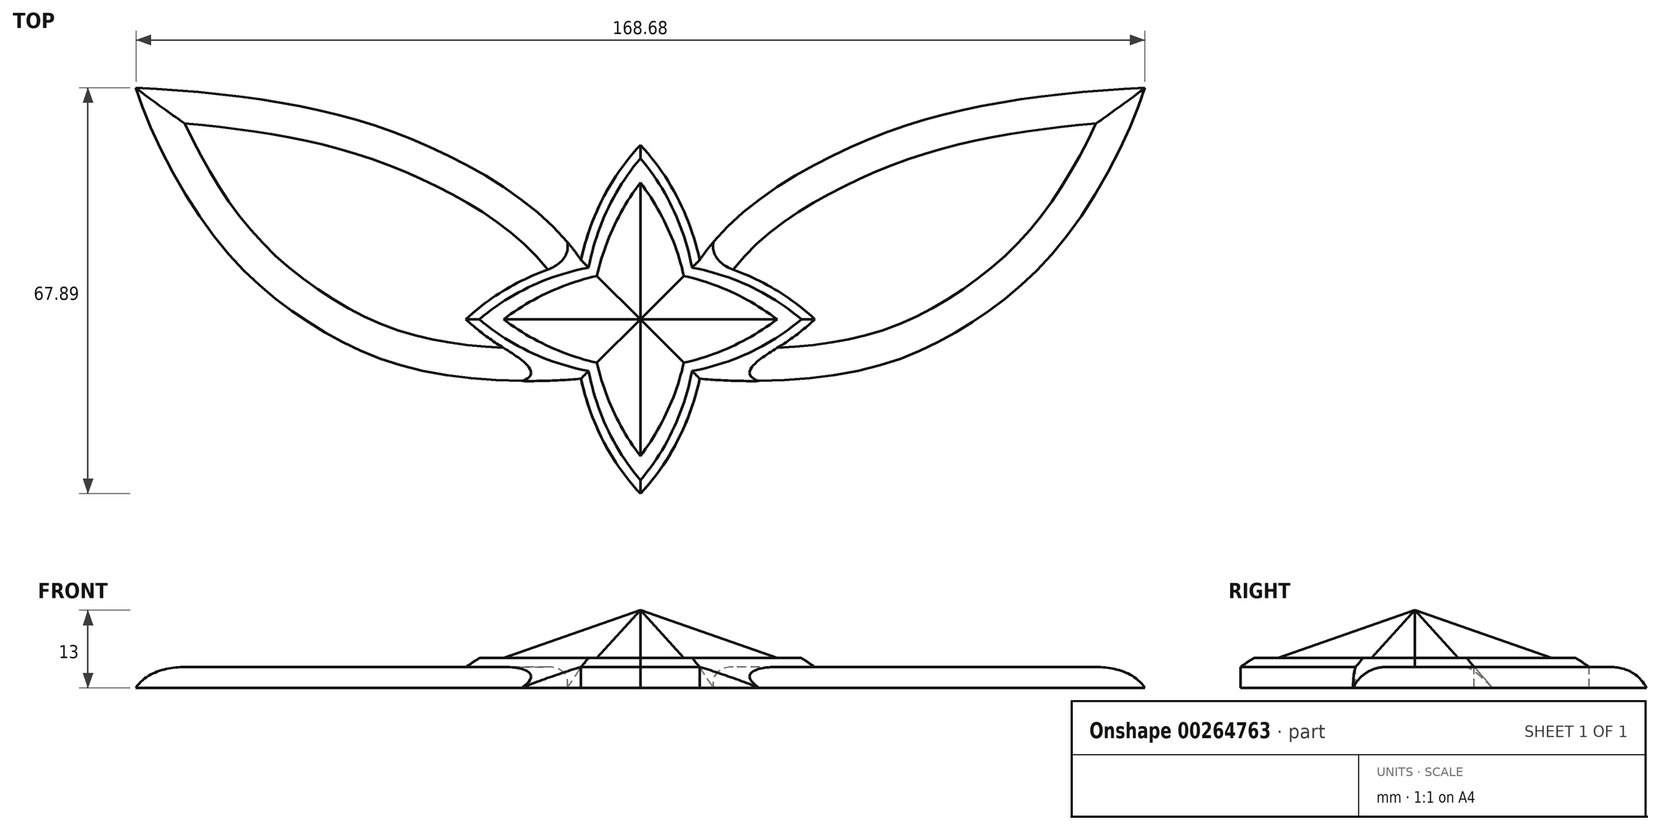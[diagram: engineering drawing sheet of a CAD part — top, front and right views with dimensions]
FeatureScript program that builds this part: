
annotation { "Feature Type Name" : "Feature", "Feature Type Description" : "" }
export const myFeature = defineFeature(function(context is Context, id is Id, definition is map)
    precondition{}
    {
        {
            var Q0;
            Q0=qCreatedBy(makeId("Top.planeOp"),FACE);
            var sketch = newSketch(context, id + "F0", { "sketchPlane" : qUnion([Q0])});
            skLineSegment(sketch, "E0", {"start": v(0, 27.96) * mm, "end": v(0, -27.04) * mm, "construction": true});
            skSolve(sketch);
        }
        {
            var Q0;
            Q0=qCreatedBy(makeId("Top.planeOp"),FACE);
            var sketch = newSketch(context, id + "F1", { "sketchPlane" : qUnion([Q0])});
            skFitSpline(sketch, "E1", {"points": [v(0, 22.87) * mm, v(-7.26, 7.26) * mm], "startDerivative": vector(-10.3, -13.5) * mm, "endDerivative": vector(-3.62, -16.65) * mm});
            skLineSegment(sketch, "E2", {"start": v(-7.26, 7.26) * mm, "end": v(0, 0) * mm, "construction": true});
            skFitSpline(sketch, "E3.MirrorCS", {"points": [v(0, 22.87) * mm, v(7.26, 7.26) * mm], "startDerivative": vector(10.3, -13.5) * mm, "endDerivative": vector(3.62, -16.65) * mm});
            skLineSegment(sketch, "E4.MirrorCS", {"start": v(7.26, 7.26) * mm, "end": v(0, 0) * mm, "construction": true});
            skFitSpline(sketch, "E5.MirrorCS", {"points": [v(-22.87, 0) * mm, v(-7.26, 7.26) * mm], "startDerivative": vector(13.5, 10.3) * mm, "endDerivative": vector(16.65, 3.62) * mm});
            skFitSpline(sketch, "E6.MirrorCS", {"points": [v(-22.87, 0) * mm, v(-7.26, -7.26) * mm], "startDerivative": vector(13.5, -10.3) * mm, "endDerivative": vector(16.65, -3.62) * mm});
            skFitSpline(sketch, "E7.MirrorCS", {"points": [v(22.87, 0) * mm, v(7.26, 7.26) * mm], "startDerivative": vector(-13.5, 10.3) * mm, "endDerivative": vector(-16.65, 3.62) * mm});
            skFitSpline(sketch, "E8.MirrorCS", {"points": [v(22.87, 0) * mm, v(7.26, -7.26) * mm], "startDerivative": vector(-13.5, -10.3) * mm, "endDerivative": vector(-16.65, -3.62) * mm});
            skFitSpline(sketch, "E9.MirrorCS", {"points": [v(0, -22.87) * mm, v(7.26, -7.26) * mm], "startDerivative": vector(10.3, 13.5) * mm, "endDerivative": vector(3.62, 16.65) * mm});
            skFitSpline(sketch, "E10.MirrorCS", {"points": [v(0, -22.87) * mm, v(-7.26, -7.26) * mm], "startDerivative": vector(-10.3, 13.5) * mm, "endDerivative": vector(-3.62, 16.65) * mm});
            skSolve(sketch);
        }
        {
            var Q0;
            Q0=qCreatedBy(makeId("Top.planeOp"),FACE);
            cPlane(context, id + "F2", {"entities" : qUnion([Q0]), "cplaneType" : CPlaneType.OFFSET, "offset" : 8 * mm, "width" : 150 * mm, "height" : 150 * mm});
        }
        {
            var Q0;
            Q0=qCreatedBy(id+"F2.planeOp",FACE);
            var sketch = newSketch(context, id + "F3", { "sketchPlane" : qUnion([Q0])});
            skPoint(sketch, "E11", {"position": v(0, 0) * mm});
            skSolve(sketch);
        }
        {
            var Q0;
            Q0=makeQuery(id+"F1.imprint","IMPRINT",FACE,{"disambiguationData":[TD([[makeQuery(id+"F1.imprint","IMPRINT",EDGE,{"derivedFrom":sQuery(id+"F1.wireOp",EDGE,"E1")}),1.0]])]});
            var Q1;
            Q1=sQuery(id+"F3.wireOp",VERTEX,"E11");
            loft(context, id + "F4", {"sheetProfilesArray" : [{ "sheetProfileEntities" : qUnion([Q0]) }, { "sheetProfileEntities" : qUnion([Q1]) }]});
        }
        {
            var Q0;
            Q0=qCreatedBy(makeId("Top.planeOp"),FACE);
            var sketch = newSketch(context, id + "F5", { "sketchPlane" : qUnion([Q0])});
            skFitSpline(sketch, "E12", {"points": [v(0, 29.16) * mm, v(-9.93, 9.93) * mm], "startDerivative": vector(-15.07, -16.03) * mm, "endDerivative": vector(-4.6, -21.32) * mm});
            skLineSegment(sketch, "E13", {"start": v(-9.93, 9.93) * mm, "end": v(0, 0) * mm, "construction": true});
            skFitSpline(sketch, "E14.MirrorCS", {"points": [v(0, 29.16) * mm, v(9.93, 9.93) * mm], "startDerivative": vector(15.07, -16.03) * mm, "endDerivative": vector(4.6, -21.32) * mm});
            skLineSegment(sketch, "E15.MirrorCS", {"start": v(9.93, 9.93) * mm, "end": v(0, 0) * mm, "construction": true});
            skFitSpline(sketch, "E16.MirrorCS", {"points": [v(-29.16, 0) * mm, v(-9.93, -9.93) * mm], "startDerivative": vector(16.03, -15.07) * mm, "endDerivative": vector(21.32, -4.6) * mm});
            skFitSpline(sketch, "E17.MirrorCS", {"points": [v(-29.16, 0) * mm, v(-9.93, 9.93) * mm], "startDerivative": vector(16.03, 15.07) * mm, "endDerivative": vector(21.32, 4.6) * mm});
            skFitSpline(sketch, "E18.MirrorCS", {"points": [v(29.16, 0) * mm, v(9.93, 9.93) * mm], "startDerivative": vector(-16.03, 15.07) * mm, "endDerivative": vector(-21.32, 4.6) * mm});
            skFitSpline(sketch, "E19.MirrorCS", {"points": [v(29.16, 0) * mm, v(9.93, -9.93) * mm], "startDerivative": vector(-16.03, -15.07) * mm, "endDerivative": vector(-21.32, -4.6) * mm});
            skFitSpline(sketch, "E20.MirrorCS", {"points": [v(0, -29.16) * mm, v(9.93, -9.93) * mm], "startDerivative": vector(15.07, 16.03) * mm, "endDerivative": vector(4.6, 21.32) * mm});
            skFitSpline(sketch, "E21.MirrorCS", {"points": [v(0, -29.16) * mm, v(-9.93, -9.93) * mm], "startDerivative": vector(-15.07, 16.03) * mm, "endDerivative": vector(-4.6, 21.32) * mm});
            skSolve(sketch);
        }
        {
            var Q0;
            Q0=makeQuery(id+"F5.imprint","IMPRINT",FACE,{"disambiguationData":[TD([[makeQuery(id+"F5.imprint","IMPRINT",EDGE,{"derivedFrom":sQuery(id+"F5.wireOp",EDGE,"E12")}),1.0]])]});
            extrude(context, id + "F6", {"entities" : qUnion([Q0]), "operationType" : NewBodyOperationType.ADD, "oppositeDirection" : true, "depth" : 5 * mm, "offsetDistance" : 25 * mm});
        }
        {
            var Q0;
            Q0=makeQuery(id+"F6.opExtrude","CAP_EDGE",EDGE,{"disambiguationData":[OSD([sQuery(id+"F5.wireOp",EDGE,"E17.MirrorCS")])],"isStart":true});
            var Q1;
            Q1=makeQuery(id+"F6.opExtrude","CAP_EDGE",EDGE,{"disambiguationData":[OSD([sQuery(id+"F5.wireOp",EDGE,"E16.MirrorCS")])],"isStart":true});
            var Q2;
            Q2=makeQuery(id+"F6.opExtrude","CAP_EDGE",EDGE,{"disambiguationData":[OSD([sQuery(id+"F5.wireOp",EDGE,"E21.MirrorCS")])],"isStart":true});
            var Q3;
            Q3=makeQuery(id+"F6.opExtrude","CAP_EDGE",EDGE,{"disambiguationData":[OSD([sQuery(id+"F5.wireOp",EDGE,"E20.MirrorCS")])],"isStart":true});
            var Q4;
            Q4=makeQuery(id+"F6.opExtrude","CAP_EDGE",EDGE,{"disambiguationData":[OSD([sQuery(id+"F5.wireOp",EDGE,"E19.MirrorCS")])],"isStart":true});
            var Q5;
            Q5=makeQuery(id+"F6.opExtrude","CAP_EDGE",EDGE,{"disambiguationData":[OSD([sQuery(id+"F5.wireOp",EDGE,"E18.MirrorCS")])],"isStart":true});
            var Q6;
            Q6=makeQuery(id+"F6.opExtrude","CAP_EDGE",EDGE,{"disambiguationData":[OSD([sQuery(id+"F5.wireOp",EDGE,"E14.MirrorCS")])],"isStart":true});
            var Q7;
            Q7=makeQuery(id+"F6.opExtrude","CAP_EDGE",EDGE,{"disambiguationData":[OSD([sQuery(id+"F5.wireOp",EDGE,"E12")])],"isStart":true});
            chamfer(context, id + "F7", {"entities" : qUnion([Q0, Q1, Q2, Q3, Q4, Q5, Q6, Q7]), "width" : 1.5 * mm, "tangentPropagation" : true});
        }
        {
            var Q0;
            Q0=makeQuery(id+"F6.opExtrude","CAP_FACE",FACE,{"disambiguationData":[OSD([sQuery(id+"F5.wireOp",EDGE,"E12"),sQuery(id+"F5.wireOp",EDGE,"E14.MirrorCS"),sQuery(id+"F5.wireOp",EDGE,"E16.MirrorCS"),sQuery(id+"F5.wireOp",EDGE,"E17.MirrorCS"),sQuery(id+"F5.wireOp",EDGE,"E18.MirrorCS"),sQuery(id+"F5.wireOp",EDGE,"E19.MirrorCS"),sQuery(id+"F5.wireOp",EDGE,"E20.MirrorCS"),sQuery(id+"F5.wireOp",EDGE,"E21.MirrorCS")])],"isStart":false});
            var sketch = newSketch(context, id + "F8", { "sketchPlane" : qUnion([Q0])});
            skFitSpline(sketch, "E22", {"points": [v(9.93, -9.93) * mm, v(32.44, -27.55) * mm, v(56.62, -35.6) * mm, v(84.34, -38.73) * mm], "startDerivative": vector(45.04, -67.4) * mm, "endDerivative": vector(83.83, -3.85) * mm});
            skFitSpline(sketch, "E23", {"points": [v(84.34, -38.73) * mm, v(71.97, -14.77) * mm, v(56.2, 0) * mm, v(38.23, 8.18) * mm, v(9.93, 9.93) * mm], "startDerivative": vector(-22.19, 74) * mm, "endDerivative": vector(-100.9, -9.41) * mm});
            skFitSpline(sketch, "E24.MirrorCS", {"points": [v(-9.93, -9.93) * mm, v(-32.44, -27.55) * mm, v(-56.62, -35.6) * mm, v(-84.34, -38.73) * mm], "startDerivative": vector(-45.04, -67.4) * mm, "endDerivative": vector(-83.83, -3.85) * mm});
            skFitSpline(sketch, "E25.MirrorCS", {"points": [v(-84.34, -38.73) * mm, v(-71.97, -14.77) * mm, v(-56.2, 0) * mm, v(-38.23, 8.18) * mm, v(-9.93, 9.93) * mm], "startDerivative": vector(22.19, 74) * mm, "endDerivative": vector(100.9, -9.41) * mm});
            skSolve(sketch);
        }
        {
            var Q0;
            Q0=makeQuery(id+"F8.imprint","IMPRINT",FACE,{"disambiguationData":[TD([[makeQuery(id+"F8.imprint","IMPRINT",EDGE,{"derivedFrom":sQuery(id+"F8.wireOp",EDGE,"E24.MirrorCS")}),-1.0]])]});
            var Q1;
            Q1=makeQuery(id+"F8.imprint","IMPRINT",FACE,{"disambiguationData":[TD([[makeQuery(id+"F8.imprint","IMPRINT",EDGE,{"derivedFrom":sQuery(id+"F8.wireOp",EDGE,"E22")}),1.0]])]});
            extrude(context, id + "F9", {"entities" : qUnion([Q0, Q1]), "operationType" : NewBodyOperationType.ADD, "oppositeDirection" : true, "depth" : 3.5 * mm, "offsetDistance" : 25 * mm});
        }
        {
            var Q0;
            Q0=makeQuery(id+"F9.opExtrude","CAP_EDGE",EDGE,{"disambiguationData":[OSD([sQuery(id+"F8.wireOp",EDGE,"E25.MirrorCS")])],"isStart":false});
            var Q1;
            Q1=makeQuery(id+"F9.opExtrude","CAP_EDGE",EDGE,{"disambiguationData":[OSD([sQuery(id+"F8.wireOp",EDGE,"E24.MirrorCS")])],"isStart":false});
            var Q2;
            Q2=makeQuery(id+"F9.opExtrude","CAP_EDGE",EDGE,{"disambiguationData":[OSD([sQuery(id+"F8.wireOp",EDGE,"E23")])],"isStart":false});
            var Q3;
            Q3=makeQuery(id+"F9.opExtrude","CAP_EDGE",EDGE,{"disambiguationData":[OSD([sQuery(id+"F8.wireOp",EDGE,"E22")])],"isStart":false});
            fillet(context, id + "F10", {"entities" : qUnion([Q0, Q1, Q2, Q3]), "tangentPropagation" : true, "radius" : 6 * mm, "defaultsChanged" : true, "vertexSettings" : [], "allowEdgeOverflow" : false});
        }
    });
